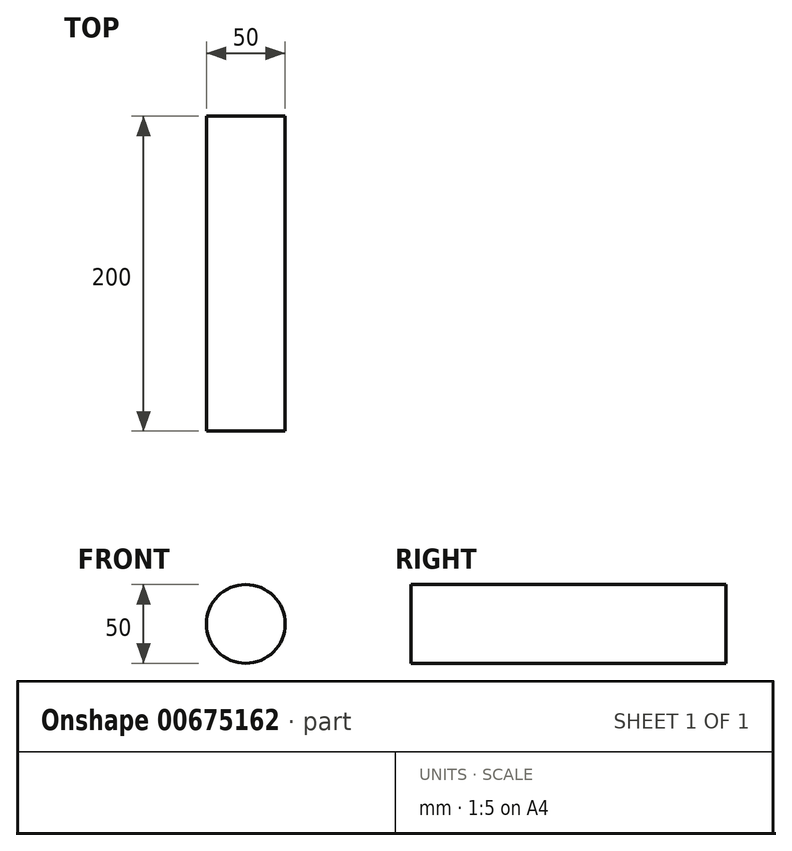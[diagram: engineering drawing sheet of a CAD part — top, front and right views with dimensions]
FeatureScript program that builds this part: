
annotation { "Feature Type Name" : "Feature", "Feature Type Description" : "" }
export const myFeature = defineFeature(function(context is Context, id is Id, definition is map)
    precondition{}
    {
        {
            var Q0;
            Q0=qCreatedBy(makeId("Front.planeOp"),FACE);
            var sketch = newSketch(context, id + "F0", { "sketchPlane" : qUnion([Q0])});
            skCircle(sketch, "E0", {"center": v(0, 0) * mm, "radius": 25 * mm});
            skSolve(sketch);
        }
        {
            var Q0;
            Q0=makeQuery(id+"F0.imprint","IMPRINT",FACE,{"disambiguationData":[TD([[makeQuery(id+"F0.imprint","IMPRINT",EDGE,{"derivedFrom":sQuery(id+"F0.wireOp",EDGE,"E0")}),1.0]])]});
            extrude(context, id + "F1", {"entities" : qUnion([Q0]), "depth" : 200 * mm, "offsetDistance" : 25 * mm});
        }
    });
